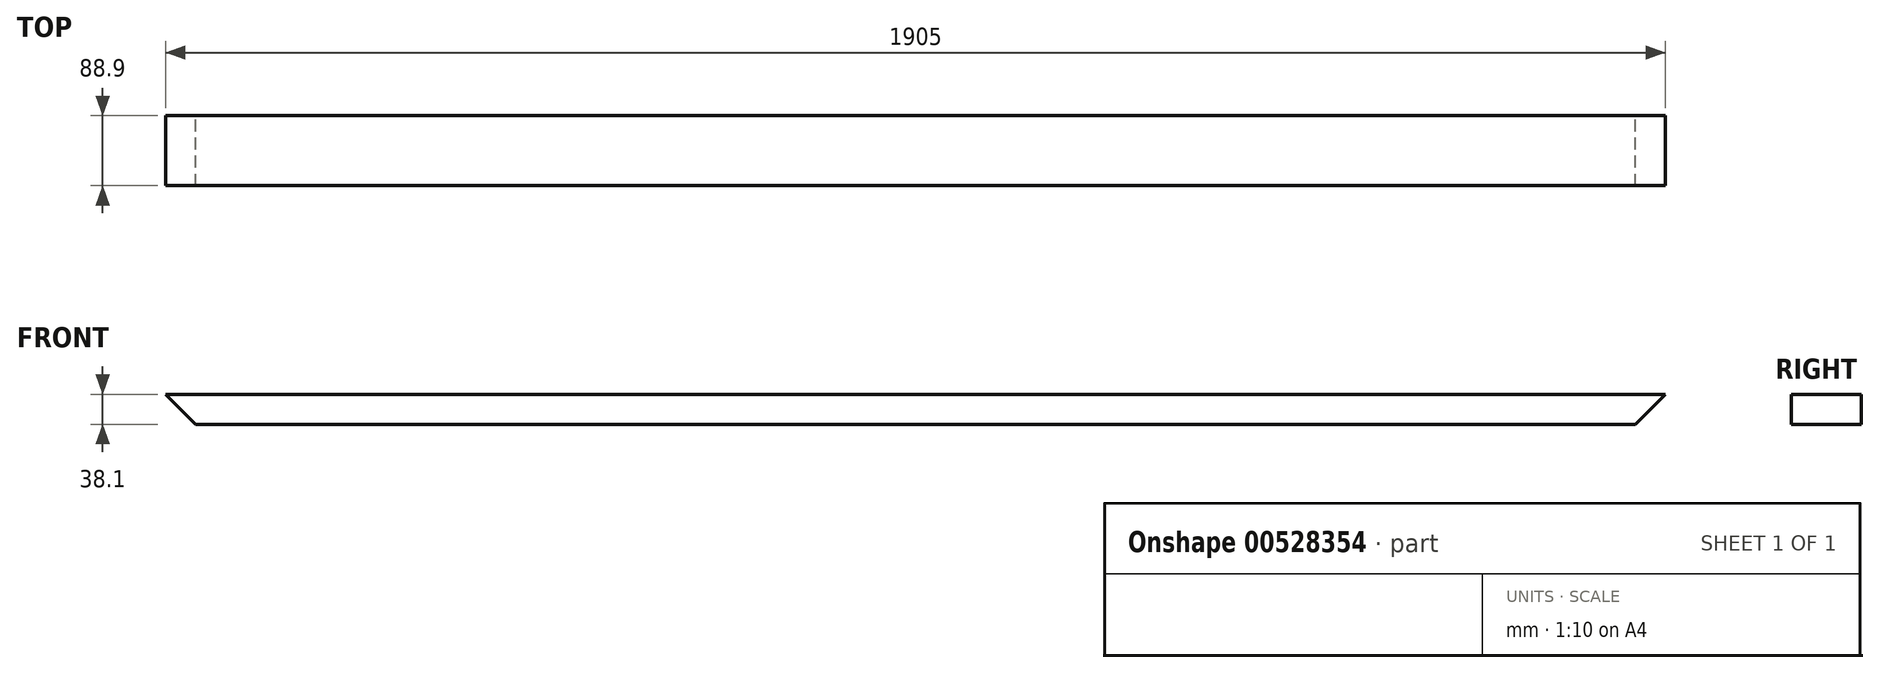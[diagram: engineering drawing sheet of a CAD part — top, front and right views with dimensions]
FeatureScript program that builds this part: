
annotation { "Feature Type Name" : "Feature", "Feature Type Description" : "" }
export const myFeature = defineFeature(function(context is Context, id is Id, definition is map)
    precondition{}
    {
        {
            var Q0;
            Q0=qCreatedBy(makeId("Front.planeOp"),FACE);
            var sketch = newSketch(context, id + "F0", { "sketchPlane" : qUnion([Q0])});
            skLineSegment(sketch, "E0", {"start": v(0, 26.7) * mm, "end": v(-1905, 26.7) * mm});
            skLineSegment(sketch, "E1", {"start": v(-1905, 26.7) * mm, "end": v(-1905, -11.4) * mm, "construction": true});
            skLineSegment(sketch, "E2", {"start": v(-1905, 26.7) * mm, "end": v(-1866.9, -11.4) * mm});
            skLineSegment(sketch, "E3", {"start": v(0, 65.3) * mm, "end": v(0, -64.84) * mm, "construction": true});
            skLineSegment(sketch, "E4", {"start": v(-1866.9, -11.4) * mm, "end": v(-38.1, -11.4) * mm});
            skLineSegment(sketch, "E5", {"start": v(-38.1, -11.4) * mm, "end": v(0, 26.7) * mm});
            skSolve(sketch);
        }
        {
            var Q0;
            Q0 = qSketchRegion(id + "F0", true);
            extrude(context, id + "F1", {"entities" : qUnion([Q0]), "depth" : 88.9 * mm, "offsetDistance" : 25.4 * mm});
        }
    });
